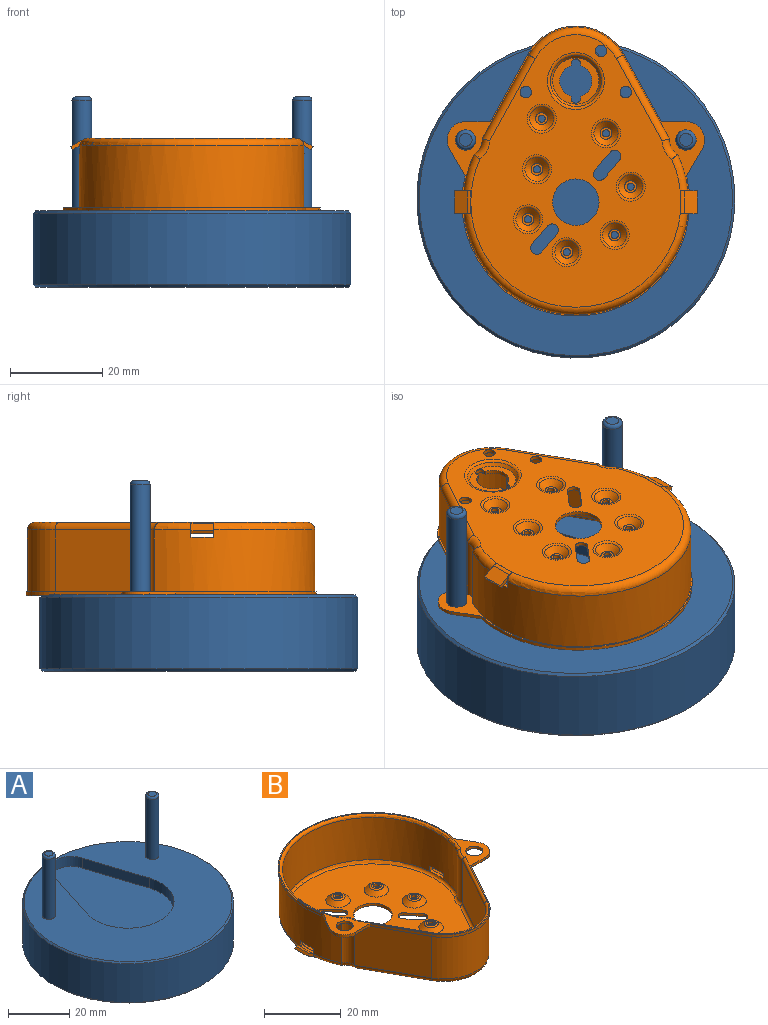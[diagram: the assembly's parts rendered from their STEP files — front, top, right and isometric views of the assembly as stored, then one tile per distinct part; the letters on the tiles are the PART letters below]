
ASSEMBLY  parts=2 mates=1
PART A: 16 faces, bbox 68.8x68.8x41.2 mm
  f0: cylinder r=34.4mm len=68.8mm, axis (0,0,-1), area 3350.2mm2, adj f14,f15
  f1: plane 67.8x67.8mm, normal (0,0,1), area 2548mm2, adj f3,f5,f9,f10,f11,f12,f15
  f2: plane 67.8x67.8mm, normal (0,0,-1), area 3610.3mm2, adj f14
  f3: cylinder r=2.15mm len=23.95mm, axis (0,0,-1), area 322.8mm2, adj f1,f8
  f4: plane 2.79x2.79mm, normal (0,0,1), area 6.1mm2, adj f8
  f5: cylinder r=2.15mm len=23.95mm, axis (0,0,-1), area 322.8mm2, adj f1,f7
  f6: plane 2.79x2.79mm, normal (0,0,1), area 6.1mm2, adj f7
  f7: torus R=1.4mm, axis (0,0,1), area 13.9mm2, adj f5,f6
  f8: torus R=1.4mm, axis (0,0,1), area 13.9mm2, adj f3,f4
  f9: plane 23.27x7.48mm, normal (0.95,-0.31,0), area 97.8mm2, adj f1,f10,f12,f13
  f10: cylinder r=15mm len=30mm, axis (0,0,1), area 225.8mm2, adj f1,f9,f11,f13
  f11: plane 23.27x7.48mm, normal (-0.95,-0.31,0), area 97.8mm2, adj f1,f10,f12,f13
  f12: cylinder r=7mm len=13.6mm, axis (0,0,1), area 74.6mm2, adj f1,f9,f11,f13
  f13: plane 48.2x30mm, normal (0,0,1), area 1033.4mm2, adj f9,f10,f11,f12
  f14: cone r=34.4mm half-angle=45deg, axis (0,0,1), area 151.7mm2, adj f0,f2
  f15: cone r=33.9mm half-angle=45deg, axis (0,0,-1), area 151.7mm2, adj f0,f1
PART B: 155 faces, bbox 56x66.6x16.1 mm
  f0: cylinder r=1.25mm len=2.5mm, axis (0,0,1), area 6.4mm2, adj f71,f101
  f1: cylinder r=1.25mm len=2.5mm, axis (0,0,1), area 6.4mm2, adj f71,f101
  f2: cylinder r=1.25mm len=2.5mm, axis (0,0,1), area 6.4mm2, adj f71,f101
  f3: cylinder r=1.35mm len=2.38mm, axis (0,0,1), area 3.4mm2, adj f71,f101,f125,f126
  f4: cylinder r=1.35mm len=2.38mm, axis (0,0,1), area 3.4mm2, adj f71,f101,f121,f123
  f5: cylinder r=5.02mm len=10.04mm, axis (0,0,1), area 25.5mm2, adj f71,f101
  f6: cylinder r=3.49mm len=6.67mm, axis (0,0,1), area 7.2mm2, adj f79,f100,f115,f116
  f7: cylinder r=0.77mm len=1.55mm, axis (0,0,1), area 3.9mm2, adj f72,f93
  f8: cylinder r=0.77mm len=1.55mm, axis (0,0,1), area 3.9mm2, adj f73,f94
  f9: cylinder r=0.77mm len=1.55mm, axis (0,0,1), area 3.9mm2, adj f78,f99
  f10: cylinder r=0.77mm len=1.55mm, axis (0,0,1), area 3.9mm2, adj f77,f98
  f11: cylinder r=0.77mm len=1.55mm, axis (0,0,1), area 3.9mm2, adj f74,f95
  f12: cylinder r=0.77mm len=1.55mm, axis (0,0,1), area 3.9mm2, adj f75,f96
  f13: cylinder r=0.77mm len=1.55mm, axis (0,0,1), area 3.9mm2, adj f76,f97
  f14: cylinder r=2.2mm len=4.4mm, axis (0,0,1), area 11.2mm2, adj f66,f92
  f15: cylinder r=2.2mm len=4.4mm, axis (0,0,1), area 11.2mm2, adj f66,f92
  f16: torus R=6.14mm, axis (0,0,1), area 27.8mm2, adj f28,f101
  f17: torus R=3.15mm, axis (0,0,1), area 10.8mm2, adj f35,f101
  f18: torus R=3.15mm, axis (0,0,1), area 10.8mm2, adj f34,f101
  f19: torus R=3.15mm, axis (0,0,1), area 10.8mm2, adj f33,f101
  f20: torus R=3.15mm, axis (0,0,1), area 10.8mm2, adj f32,f101
  f21: torus R=3.15mm, axis (0,0,1), area 10.8mm2, adj f31,f101
  f22: torus R=3.15mm, axis (0,0,1), area 10.8mm2, adj f30,f101
  f23: torus R=3.15mm, axis (0,0,1), area 10.8mm2, adj f29,f101
  f24: torus R=3.6mm, axis (0,0,1), area 5.4mm2, adj f25,f66,f69,f113
  f25: torus R=24.32mm, axis (0,0,1), area 120mm2, adj f24,f57,f66,f110
  f26: cylinder r=3.59mm len=13.39mm, axis (0,0,-1), area 53.2mm2, adj f58,f92,f104,f108
  f27: torus R=5.2mm, axis (0,0,1), area 10.6mm2, adj f65,f101,f105,f107
  f28: cone r=4.74mm half-angle=35.4deg, axis (0,0,-1), area 28.8mm2, adj f16,f100
  f29: cone r=1.05mm half-angle=46.9deg, axis (0,0,-1), area 22mm2, adj f23,f99
  f30: cone r=1.05mm half-angle=46.9deg, axis (0,0,-1), area 22mm2, adj f22,f98
  f31: cone r=1.05mm half-angle=46.9deg, axis (0,0,-1), area 22mm2, adj f21,f97
  f32: cone r=1.05mm half-angle=46.9deg, axis (0,0,-1), area 22mm2, adj f20,f96
  f33: cone r=1.05mm half-angle=46.9deg, axis (0,0,-1), area 22mm2, adj f19,f95
  f34: cone r=1.05mm half-angle=46.9deg, axis (0,0,-1), area 22mm2, adj f18,f94
  f35: cone r=1.05mm half-angle=46.9deg, axis (0,0,-1), area 22mm2, adj f17,f93
  f36: cylinder r=4mm len=6mm, axis (0,0,1), area 6.8mm2, adj f66,f89,f90,f92
  f37: cylinder r=24.64mm len=49.27mm, axis (0,0,1), area 72mm2, adj f66,f88,f89,f92
  f38: torus R=1.28mm, axis (0,0,1), area 5.9mm2, adj f51,f76
  f39: torus R=1.28mm, axis (0,0,1), area 5.9mm2, adj f52,f75
  f40: torus R=1.28mm, axis (0,0,1), area 5.9mm2, adj f53,f74
  f41: torus R=1.28mm, axis (0,0,1), area 5.9mm2, adj f50,f77
  f42: torus R=1.28mm, axis (0,0,1), area 5.9mm2, adj f49,f78
  f43: torus R=1.28mm, axis (0,0,1), area 5.9mm2, adj f54,f73
  f44: torus R=1.28mm, axis (0,0,1), area 5.9mm2, adj f55,f72
  f45: torus R=4.99mm, axis (0,0,1), area 25.6mm2, adj f48,f79
  f46: torus R=5.2mm, axis (0,0,1), area 5.6mm2, adj f47,f69,f71,f83
  f47: torus R=22.72mm, axis (0,0,1), area 116.5mm2, adj f46,f57,f71,f81,f140,f153
  f48: cone r=5.41mm half-angle=35.4deg, axis (0,0,-1), area 32.4mm2, adj f45,f71
  f49: cone r=1.6mm half-angle=46.9deg, axis (0,0,-1), area 28.3mm2, adj f42,f71
  f50: cone r=1.6mm half-angle=46.9deg, axis (0,0,-1), area 28.3mm2, adj f41,f71
  f51: cone r=1.6mm half-angle=46.9deg, axis (0,0,-1), area 28.3mm2, adj f38,f71
  f52: cone r=1.6mm half-angle=46.9deg, axis (0,0,-1), area 28.3mm2, adj f39,f71
  f53: cone r=1.6mm half-angle=46.9deg, axis (0,0,-1), area 28.3mm2, adj f40,f71
  f54: cone r=1.6mm half-angle=46.9deg, axis (0,0,-1), area 28.3mm2, adj f43,f71
  f55: cone r=1.6mm half-angle=46.9deg, axis (0,0,-1), area 28.3mm2, adj f44,f71
  f56: cylinder r=4.4mm len=13.4mm, axis (0,0,-1), area 58.3mm2, adj f57,f68,f81,f110
  f57: cylinder r=23.53mm len=47.05mm, axis (0,0,-1), area 1245mm2, adj f25,f47,f56,f69,f135,f136,f137,f149
  f58: cylinder r=24.33mm len=48.67mm, axis (0,0,-1), area 1294mm2, adj f26,f61,f64,f65,f92,f107,f135,f136
  f59: plane 1.79x0.14mm, normal (-0.5,0,0.87), area 0.1mm2, adj f64,f148,f153
  f60: plane 1.79x0.14mm, normal (-0.5,0,0.87), area 0.1mm2, adj f61,f147,f153
  f61: torus R=22.72mm, axis (0,0,1), area 176.6mm2, adj f58,f60,f63,f101,f128,f133,f140,f142
  f62: plane 4.93x1.5mm, normal (0.5,0,0.87), area 8.5mm2, adj f130,f133,f134,f138,f139
  f63: plane 1.79x0.14mm, normal (0.5,0,0.87), area 0.1mm2, adj f61,f133,f140
  f64: torus R=22.72mm, axis (0,0,1), area 19.8mm2, adj f58,f59,f101,f104,f143,f148,f153
  f65: torus R=22.72mm, axis (0,0,1), area 19.9mm2, adj f27,f58,f101,f131,f132,f134,f140
  f66: plane 62.76x55.65mm, normal (0,0,1), area 140.4mm2, adj f14,f15,f24,f25,f36,f37,f84,f85
  f67: cylinder r=10.82mm len=18.93mm, axis (0,0,-1), area 308.8mm2, adj f68,f70,f82,f112
  f68: plane 17.95x13.4mm, normal (-0.87,0.48,0), area 275.1mm2, adj f56,f67,f80,f111
  f69: cylinder r=4.4mm len=13.4mm, axis (0,0,-1), area 58.3mm2, adj f24,f46,f57,f70
  f70: plane 17.95x13.4mm, normal (0.87,0.48,0), area 275.1mm2, adj f67,f69,f83,f113
  f71: plane 58.94x45.45mm, normal (0,0,1), area 1456.7mm2, adj f0,f1,f2,f3,f4,f5,f46,f47
  f72: plane 2.57x2.57mm, normal (0,0,1), area 3.3mm2, adj f7,f44
  f73: plane 2.57x2.57mm, normal (0,0,1), area 3.3mm2, adj f8,f43
  f74: plane 2.57x2.57mm, normal (0,0,1), area 3.3mm2, adj f11,f40
  f75: plane 2.57x2.57mm, normal (0,0,1), area 3.3mm2, adj f12,f39
  f76: plane 2.57x2.57mm, normal (0,0,1), area 3.3mm2, adj f13,f38
  f77: plane 2.57x2.57mm, normal (0,0,1), area 3.3mm2, adj f10,f41
  f78: plane 2.57x2.57mm, normal (0,0,1), area 3.3mm2, adj f9,f42
  f79: plane 9.98x9.98mm, normal (0,0,1), area 35.5mm2, adj f6,f45,f114,f115,f116,f117,f118,f119
  f80: cylinder r=0.8mm len=18.34mm, axis (0.48,0.87,0), area 25.7mm2, adj f68,f71,f81,f82
  f81: torus R=5.2mm, axis (0,0,1), area 5.6mm2, adj f47,f56,f71,f80
  f82: torus R=10.02mm, axis (0,0,1), area 28.2mm2, adj f67,f71,f80,f83
  f83: cylinder r=0.8mm len=18.34mm, axis (0.48,-0.87,0), area 25.7mm2, adj f46,f70,f71,f82
  f84: cylinder r=11.93mm len=20.88mm, axis (0,0,1), area 20.6mm2, adj f66,f85,f91,f92
  f85: plane 14.51x8.05mm, normal (-0.87,-0.48,0), area 13.4mm2, adj f66,f84,f86,f92
  f86: plane 5.34x0.81mm, normal (0,-1,0), area 4.3mm2, adj f66,f85,f87,f92
  f87: cylinder r=4mm len=6mm, axis (0,0,1), area 6.8mm2, adj f66,f86,f88,f92
  f88: plane 5.75x3.32mm, normal (-0.87,0.5,0), area 5.4mm2, adj f37,f66,f87,f92
  f89: plane 5.75x3.32mm, normal (0.87,0.5,0), area 5.4mm2, adj f36,f37,f66,f92
  f90: plane 5.34x0.81mm, normal (0,-1,0), area 4.3mm2, adj f36,f66,f91,f92
  f91: plane 14.51x8.05mm, normal (0.87,-0.48,0), area 13.4mm2, adj f66,f84,f90,f92
  f92: plane 62.76x55.65mm, normal (0,0,-1), area 138.7mm2, adj f14,f15,f26,f36,f37,f58,f84,f85
  f93: plane 2.56x2.56mm, normal (0,0,-1), area 3.3mm2, adj f7,f35
  f94: plane 2.56x2.56mm, normal (0,0,-1), area 3.3mm2, adj f8,f34
  f95: plane 2.56x2.56mm, normal (0,0,-1), area 3.3mm2, adj f11,f33
  f96: plane 2.56x2.56mm, normal (0,0,-1), area 3.3mm2, adj f12,f32
  f97: plane 2.56x2.56mm, normal (0,0,-1), area 3.3mm2, adj f13,f31
  f98: plane 2.56x2.56mm, normal (0,0,-1), area 3.3mm2, adj f10,f30
  f99: plane 2.56x2.56mm, normal (0,0,-1), area 3.3mm2, adj f9,f29
  f100: plane 9.97x9.97mm, normal (0,0,-1), area 35.3mm2, adj f6,f28,f114,f115,f116,f117,f118,f119
  f101: plane 58.94x45.45mm, normal (0,0,-1), area 1457.4mm2, adj f0,f1,f2,f3,f4,f5,f16,f17
  f102: torus R=10.02mm, axis (0,0,1), area 59.5mm2, adj f101,f103,f105,f109
  f103: cylinder r=1.61mm len=18.93mm, axis (0.48,0.87,0), area 51.9mm2, adj f101,f102,f104,f108
  f104: torus R=5.2mm, axis (0,0,1), area 10.6mm2, adj f26,f64,f101,f103
  f105: cylinder r=1.61mm len=18.93mm, axis (0.48,-0.87,0), area 52mm2, adj f27,f101,f102,f106
  f106: plane 18.15x13.39mm, normal (-0.87,-0.48,0), area 277.9mm2, adj f92,f105,f107,f109
  f107: cylinder r=3.59mm len=13.39mm, axis (0,0,-1), area 53.2mm2, adj f27,f58,f92,f106
  f108: plane 18.15x13.39mm, normal (0.87,-0.48,0), area 277.9mm2, adj f26,f92,f103,f109
  f109: cylinder r=11.63mm len=20.35mm, axis (0,0,-1), area 331.7mm2, adj f92,f102,f106,f108
  f110: torus R=3.6mm, axis (0,0,1), area 5.4mm2, adj f25,f56,f66,f111
  f111: cylinder r=0.8mm len=18.53mm, axis (0.48,0.87,0), area 25.9mm2, adj f66,f68,f110,f112
  f112: torus R=11.62mm, axis (0,0,1), area 29.7mm2, adj f66,f67,f111,f113
  f113: cylinder r=0.8mm len=18.53mm, axis (0.48,-0.87,0), area 25.9mm2, adj f24,f66,f70,f112
  f114: cylinder r=1.03mm len=2.05mm, axis (0,0,1), area 2.6mm2, adj f79,f100,f115,f120
  f115: plane 0.81x0.42mm, normal (-1,0,0), area 0.3mm2, adj f6,f79,f100,f114
  f116: plane 0.81x0.42mm, normal (-1,0,0), area 0.3mm2, adj f6,f79,f100,f117
  f117: cylinder r=1.03mm len=2.05mm, axis (0,0,1), area 2.6mm2, adj f79,f100,f116,f118
  f118: plane 0.81x0.42mm, normal (1,0,0), area 0.3mm2, adj f79,f100,f117,f119
  f119: cylinder r=3.49mm len=6.67mm, axis (0,0,1), area 7.2mm2, adj f79,f100,f118,f120
  f120: plane 0.81x0.42mm, normal (1,0,0), area 0.3mm2, adj f79,f100,f114,f119
  f121: plane 3.85x3.27mm, normal (0.76,0.65,0), area 4.1mm2, adj f4,f71,f101,f122
  f122: cylinder r=1.35mm len=2.38mm, axis (0,0,1), area 3.4mm2, adj f71,f101,f121,f123
  f123: plane 3.85x3.27mm, normal (-0.76,-0.65,0), area 4.1mm2, adj f4,f71,f101,f122
  f124: cylinder r=1.35mm len=2.38mm, axis (0,0,1), area 3.4mm2, adj f71,f101,f125,f126
  f125: plane 3.85x3.27mm, normal (-0.76,-0.65,0), area 4.1mm2, adj f3,f71,f101,f124
  f126: plane 3.85x3.27mm, normal (0.76,0.65,0), area 4.1mm2, adj f3,f71,f101,f124
  f127: cylinder r=1.61mm len=4.93mm, axis (0,-1,0), area 4.2mm2, adj f128,f129,f132,f133,f134
  f128: plane 2.78x0.32mm, normal (1,0,0), area 0mm2, adj f61,f127,f133
  f129: plane 4.93x2.71mm, normal (-0.5,0,-0.87), area 15.4mm2, adj f127,f130,f133,f134
  f130: plane 4.93x0.7mm, normal (-0.87,0,0.5), area 4mm2, adj f62,f129,f133,f134
  f131: plane 1.79x0.14mm, normal (0.5,0,0.87), area 0.1mm2, adj f65,f134,f140
  f132: plane 2.78x0.32mm, normal (1,0,0), area 0mm2, adj f65,f127,f134
  f133: plane 3.58x2.55mm, normal (0,1,0), area 1.9mm2, adj f61,f62,f63,f127,f128,f129,f130,f139
  f134: plane 3.58x2.55mm, normal (0,-1,0), area 1.9mm2, adj f62,f65,f127,f129,f130,f131,f132,f138
  f135: plane 4.93x0.94mm, normal (0,0,-1), area 4mm2, adj f57,f58,f136,f137
  f136: plane 1.64x0.81mm, normal (0,-1,0), area 1.3mm2, adj f57,f58,f135,f140
  f137: plane 1.64x0.81mm, normal (0,1,0), area 1.3mm2, adj f57,f58,f135,f140
  f138: plane 2.46x0.01mm, normal (1,0,0), area 0mm2, adj f62,f134,f140
  f139: plane 2.46x0.01mm, normal (1,0,0), area 0mm2, adj f62,f133,f140
  f140: plane 4.93x0.94mm, normal (0,0,1), area 4mm2, adj f47,f61,f63,f65,f131,f133,f134,f136
  f141: cylinder r=1.61mm len=4.93mm, axis (0,-1,0), area 4.2mm2, adj f142,f143,f146,f147,f148
  f142: plane 2.78x0.32mm, normal (-1,0,0), area 0mm2, adj f61,f141,f147
  f143: plane 2.78x0.32mm, normal (-1,0,0), area 0mm2, adj f64,f141,f148
  f144: plane 4.93x1.5mm, normal (-0.5,0,0.87), area 8.5mm2, adj f145,f147,f148,f152,f154
  f145: plane 4.93x0.7mm, normal (0.87,0,0.5), area 4mm2, adj f144,f146,f147,f148
  f146: plane 4.93x2.71mm, normal (0.5,0,-0.87), area 15.4mm2, adj f141,f145,f147,f148
  f147: plane 3.58x2.55mm, normal (0,1,0), area 1.9mm2, adj f60,f61,f141,f142,f144,f145,f146,f153
  f148: plane 3.58x2.55mm, normal (0,-1,0), area 1.9mm2, adj f59,f64,f141,f143,f144,f145,f146,f152
  f149: plane 4.93x0.94mm, normal (0,0,-1), area 4mm2, adj f57,f58,f150,f151
  f150: plane 1.64x0.81mm, normal (0,1,0), area 1.3mm2, adj f57,f58,f149,f153
  f151: plane 1.64x0.81mm, normal (0,-1,0), area 1.3mm2, adj f57,f58,f149,f153
  f152: plane 2.46x0.01mm, normal (-1,0,0), area 0mm2, adj f144,f148,f153
  f153: plane 4.93x0.94mm, normal (0,0,1), area 4mm2, adj f47,f59,f60,f61,f64,f147,f148,f150
  f154: plane 2.46x0.01mm, normal (-1,0,0), area 0mm2, adj f144,f147,f153
PLACE A t=(-30.05,-3.09,0.79)mm
PLACE B rot(axis=(1,0,0),180deg) t=(-30.06,-3.83,32.16)mm
MATE slider B.f14 <-> A.f3  axis (0,0,-1) through (-53.88,9.63,17.16)mm
